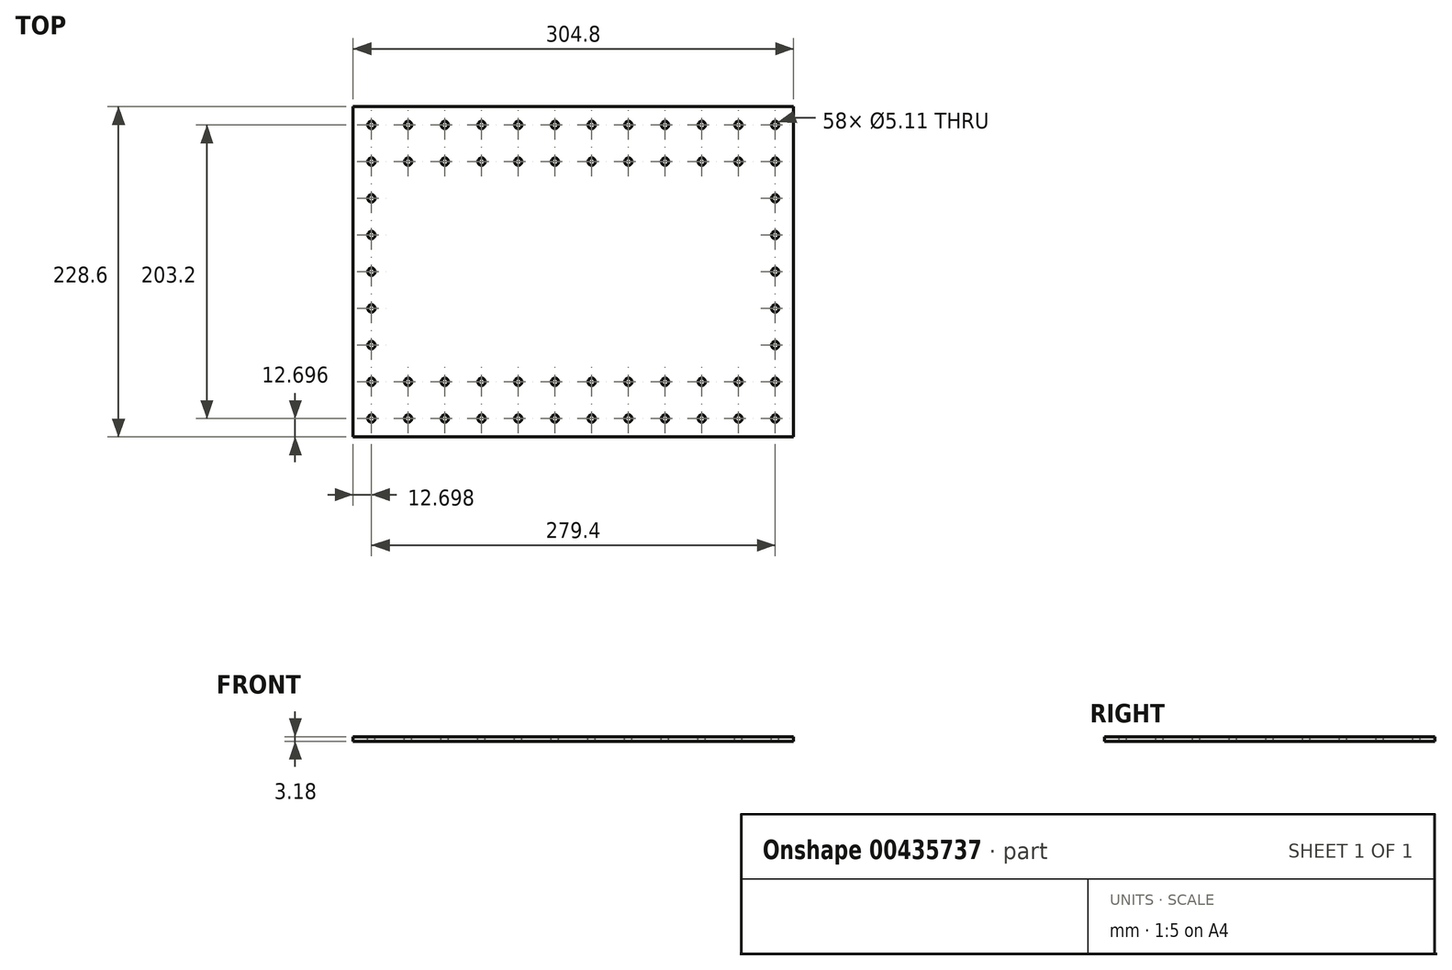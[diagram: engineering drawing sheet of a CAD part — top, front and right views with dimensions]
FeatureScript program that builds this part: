
annotation { "Feature Type Name" : "Feature", "Feature Type Description" : "" }
export const myFeature = defineFeature(function(context is Context, id is Id, definition is map)
    precondition{}
    {
        {
            var Q0;
            Q0=qCreatedBy(makeId("Top.planeOp"),FACE);
            var sketch = newSketch(context, id + "F0", { "sketchPlane" : qUnion([Q0])});
            skLineSegment(sketch, "E0.bottom", {"start": v(-91.98, 188.02) * mm, "end": v(212.82, 188.02) * mm});
            skLineSegment(sketch, "E0.top", {"start": v(-91.98, -40.58) * mm, "end": v(212.82, -40.58) * mm});
            skLineSegment(sketch, "E0.left", {"start": v(-91.98, 188.02) * mm, "end": v(-91.98, -40.58) * mm});
            skLineSegment(sketch, "E0.right", {"start": v(212.82, 188.02) * mm, "end": v(212.82, -40.58) * mm});
            skSolve(sketch);
        }
        {
            var Q0;
            Q0 = qSketchRegion(id + "F0", true);
            extrude(context, id + "F1", {"entities" : qUnion([Q0]), "depth" : 3.17 * mm});
        }
        {
            var Q0;
            Q0=makeQuery(id+"F1.opExtrude","CAP_FACE",FACE,{"disambiguationData":[OSD([sQuery(id+"F0.wireOp",EDGE,"E0.bottom"),sQuery(id+"F0.wireOp",EDGE,"E0.top"),sQuery(id+"F0.wireOp",EDGE,"E0.left"),sQuery(id+"F0.wireOp",EDGE,"E0.right")])],"isStart":false});
            var sketch = newSketch(context, id + "F2", { "sketchPlane" : qUnion([Q0])});
            skCircle(sketch, "E1", {"center": v(-79.28, 175.32) * mm, "radius": 2.55 * mm});
            skCircle(sketch, "E2.1.0.0", {"center": v(-53.88, 175.32) * mm, "radius": 2.55 * mm});
            skCircle(sketch, "E2.2.0.0", {"center": v(-28.48, 175.32) * mm, "radius": 2.55 * mm});
            skCircle(sketch, "E2.3.0.0", {"center": v(-3.08, 175.32) * mm, "radius": 2.55 * mm});
            skCircle(sketch, "E2.4.0.0", {"center": v(22.32, 175.32) * mm, "radius": 2.55 * mm});
            skCircle(sketch, "E2.5.0.0", {"center": v(47.72, 175.32) * mm, "radius": 2.55 * mm});
            skCircle(sketch, "E2.6.0.0", {"center": v(73.12, 175.32) * mm, "radius": 2.55 * mm});
            skCircle(sketch, "E2.7.0.0", {"center": v(98.52, 175.32) * mm, "radius": 2.55 * mm});
            skCircle(sketch, "E2.8.0.0", {"center": v(123.92, 175.32) * mm, "radius": 2.55 * mm});
            skCircle(sketch, "E2.9.0.0", {"center": v(149.32, 175.32) * mm, "radius": 2.55 * mm});
            skCircle(sketch, "E2.10.0.0", {"center": v(174.72, 175.32) * mm, "radius": 2.55 * mm});
            skCircle(sketch, "E2.11.0.0", {"center": v(200.12, 175.32) * mm, "radius": 2.55 * mm});
            skLineSegment(sketch, "E2.direction1", {"start": v(-79.28, 175.32) * mm, "end": v(-53.88, 175.32) * mm, "construction": true});
            skCircle(sketch, "E3.0.1.0", {"center": v(200.12, 149.92) * mm, "radius": 2.55 * mm});
            skCircle(sketch, "E3.0.2.0", {"center": v(200.12, 124.52) * mm, "radius": 2.55 * mm});
            skCircle(sketch, "E3.0.3.0", {"center": v(200.12, 99.12) * mm, "radius": 2.55 * mm});
            skCircle(sketch, "E3.0.4.0", {"center": v(200.12, 73.72) * mm, "radius": 2.55 * mm});
            skCircle(sketch, "E3.0.5.0", {"center": v(200.12, 48.32) * mm, "radius": 2.55 * mm});
            skCircle(sketch, "E3.0.6.0", {"center": v(200.12, 22.92) * mm, "radius": 2.55 * mm});
            skCircle(sketch, "E3.0.7.0", {"center": v(200.12, -2.48) * mm, "radius": 2.55 * mm});
            skCircle(sketch, "E3.0.8.0", {"center": v(200.12, -27.88) * mm, "radius": 2.55 * mm});
            skLineSegment(sketch, "E3.direction1", {"start": v(200.12, 175.32) * mm, "end": v(225.52, 175.32) * mm, "construction": true});
            skLineSegment(sketch, "E3.direction2", {"start": v(200.12, 175.32) * mm, "end": v(200.12, 149.92) * mm, "construction": true});
            skCircle(sketch, "E4.1.0.0", {"center": v(174.72, -27.88) * mm, "radius": 2.55 * mm});
            skCircle(sketch, "E4.2.0.0", {"center": v(149.32, -27.88) * mm, "radius": 2.55 * mm});
            skCircle(sketch, "E4.3.0.0", {"center": v(123.92, -27.88) * mm, "radius": 2.55 * mm});
            skCircle(sketch, "E4.4.0.0", {"center": v(98.52, -27.88) * mm, "radius": 2.55 * mm});
            skCircle(sketch, "E4.5.0.0", {"center": v(73.12, -27.88) * mm, "radius": 2.55 * mm});
            skCircle(sketch, "E4.6.0.0", {"center": v(47.72, -27.88) * mm, "radius": 2.55 * mm});
            skCircle(sketch, "E4.7.0.0", {"center": v(22.32, -27.88) * mm, "radius": 2.55 * mm});
            skCircle(sketch, "E4.8.0.0", {"center": v(-3.08, -27.88) * mm, "radius": 2.55 * mm});
            skCircle(sketch, "E4.9.0.0", {"center": v(-28.48, -27.88) * mm, "radius": 2.55 * mm});
            skCircle(sketch, "E4.10.0.0", {"center": v(-53.88, -27.88) * mm, "radius": 2.55 * mm});
            skCircle(sketch, "E4.11.0.0", {"center": v(-79.28, -27.88) * mm, "radius": 2.55 * mm});
            skLineSegment(sketch, "E4.direction1", {"start": v(200.12, -27.88) * mm, "end": v(174.72, -27.88) * mm, "construction": true});
            skCircle(sketch, "E5.0.1.0", {"center": v(-79.28, -2.48) * mm, "radius": 2.55 * mm});
            skCircle(sketch, "E5.0.2.0", {"center": v(-79.28, 22.92) * mm, "radius": 2.55 * mm});
            skCircle(sketch, "E5.0.3.0", {"center": v(-79.28, 48.32) * mm, "radius": 2.55 * mm});
            skCircle(sketch, "E5.0.4.0", {"center": v(-79.28, 73.72) * mm, "radius": 2.55 * mm});
            skCircle(sketch, "E5.0.5.0", {"center": v(-79.28, 99.12) * mm, "radius": 2.55 * mm});
            skCircle(sketch, "E5.0.6.0", {"center": v(-79.28, 124.52) * mm, "radius": 2.55 * mm});
            skCircle(sketch, "E5.0.7.0", {"center": v(-79.28, 149.92) * mm, "radius": 2.55 * mm});
            skLineSegment(sketch, "E5.direction1", {"start": v(-79.28, -27.88) * mm, "end": v(-53.88, -27.88) * mm, "construction": true});
            skLineSegment(sketch, "E5.direction2", {"start": v(-79.28, -27.88) * mm, "end": v(-79.28, -2.48) * mm, "construction": true});
            skCircle(sketch, "E6.1.0.0", {"center": v(174.72, 149.92) * mm, "radius": 2.55 * mm});
            skCircle(sketch, "E6.2.0.0", {"center": v(149.32, 149.92) * mm, "radius": 2.55 * mm});
            skCircle(sketch, "E6.3.0.0", {"center": v(123.92, 149.92) * mm, "radius": 2.55 * mm});
            skCircle(sketch, "E6.4.0.0", {"center": v(98.52, 149.92) * mm, "radius": 2.55 * mm});
            skCircle(sketch, "E6.5.0.0", {"center": v(73.12, 149.92) * mm, "radius": 2.55 * mm});
            skCircle(sketch, "E6.6.0.0", {"center": v(47.72, 149.92) * mm, "radius": 2.55 * mm});
            skCircle(sketch, "E6.7.0.0", {"center": v(22.32, 149.92) * mm, "radius": 2.55 * mm});
            skCircle(sketch, "E6.8.0.0", {"center": v(-3.08, 149.92) * mm, "radius": 2.55 * mm});
            skCircle(sketch, "E6.9.0.0", {"center": v(-28.48, 149.92) * mm, "radius": 2.55 * mm});
            skCircle(sketch, "E6.10.0.0", {"center": v(-53.88, 149.92) * mm, "radius": 2.55 * mm});
            skLineSegment(sketch, "E6.direction1", {"start": v(200.12, 149.92) * mm, "end": v(174.72, 149.92) * mm, "construction": true});
            skCircle(sketch, "E7.1.0.0", {"center": v(174.72, -2.48) * mm, "radius": 2.55 * mm});
            skCircle(sketch, "E7.2.0.0", {"center": v(149.32, -2.48) * mm, "radius": 2.55 * mm});
            skCircle(sketch, "E7.3.0.0", {"center": v(123.92, -2.48) * mm, "radius": 2.55 * mm});
            skCircle(sketch, "E7.4.0.0", {"center": v(98.52, -2.48) * mm, "radius": 2.55 * mm});
            skCircle(sketch, "E7.5.0.0", {"center": v(73.12, -2.48) * mm, "radius": 2.55 * mm});
            skCircle(sketch, "E7.6.0.0", {"center": v(47.72, -2.48) * mm, "radius": 2.55 * mm});
            skCircle(sketch, "E7.7.0.0", {"center": v(22.32, -2.48) * mm, "radius": 2.55 * mm});
            skCircle(sketch, "E7.8.0.0", {"center": v(-3.08, -2.48) * mm, "radius": 2.55 * mm});
            skCircle(sketch, "E7.9.0.0", {"center": v(-28.48, -2.48) * mm, "radius": 2.55 * mm});
            skCircle(sketch, "E7.10.0.0", {"center": v(-53.88, -2.48) * mm, "radius": 2.55 * mm});
            skLineSegment(sketch, "E7.direction1", {"start": v(200.12, -2.48) * mm, "end": v(174.72, -2.48) * mm, "construction": true});
            skSolve(sketch);
        }
        {
            var Q0;
            Q0=sQuery(id+"F2.wireOp",VERTEX,"E4.9.0.0.center");
            var Q1;
            Q1=sQuery(id+"F2.wireOp",VERTEX,"E6.4.0.0.center");
            var Q2;
            Q2=sQuery(id+"F2.wireOp",VERTEX,"E5.direction2.start");
            var Q3;
            Q3=sQuery(id+"F2.wireOp",VERTEX,"E3.0.4.0.center");
            var Q4;
            Q4=sQuery(id+"F2.wireOp",VERTEX,"E2.6.0.0.center");
            var Q5;
            Q5=sQuery(id+"F2.wireOp",VERTEX,"E2.9.0.0.center");
            var Q6;
            Q6=sQuery(id+"F2.wireOp",VERTEX,"E2.8.0.0.center");
            var Q7;
            Q7=sQuery(id+"F2.wireOp",VERTEX,"E5.direction2.end");
            var Q8;
            Q8=sQuery(id+"F2.wireOp",VERTEX,"E7.direction1.end");
            var Q9;
            Q9=sQuery(id+"F2.wireOp",VERTEX,"E3.0.7.0.center");
            var Q10;
            Q10=sQuery(id+"F2.wireOp",VERTEX,"E7.3.0.0.center");
            var Q11;
            Q11=sQuery(id+"F2.wireOp",VERTEX,"E3.0.5.0.center");
            var Q12;
            Q12=sQuery(id+"F2.wireOp",VERTEX,"E2.2.0.0.center");
            var Q13;
            Q13=sQuery(id+"F2.wireOp",VERTEX,"E7.8.0.0.center");
            var Q14;
            Q14=sQuery(id+"F2.wireOp",VERTEX,"E6.direction1.start");
            var Q15;
            Q15=sQuery(id+"F2.wireOp",VERTEX,"E4.5.0.0.center");
            var Q16;
            Q16=sQuery(id+"F2.wireOp",VERTEX,"E3.0.6.0.center");
            var Q17;
            Q17=sQuery(id+"F2.wireOp",VERTEX,"E6.7.0.0.center");
            var Q18;
            Q18=sQuery(id+"F2.wireOp",VERTEX,"E7.9.0.0.center");
            var Q19;
            Q19=sQuery(id+"F2.wireOp",VERTEX,"E4.3.0.0.center");
            var Q20;
            Q20=sQuery(id+"F2.wireOp",VERTEX,"E4.4.0.0.center");
            var Q21;
            Q21=sQuery(id+"F2.wireOp",VERTEX,"E2.7.0.0.center");
            var Q22;
            Q22=sQuery(id+"F2.wireOp",VERTEX,"E6.3.0.0.center");
            var Q23;
            Q23=sQuery(id+"F2.wireOp",VERTEX,"E1.center");
            var Q24;
            Q24=sQuery(id+"F2.wireOp",VERTEX,"E6.direction1.end");
            var Q25;
            Q25=sQuery(id+"F2.wireOp",VERTEX,"E6.10.0.0.center");
            var Q26;
            Q26=sQuery(id+"F2.wireOp",VERTEX,"E7.7.0.0.center");
            var Q27;
            Q27=sQuery(id+"F2.wireOp",VERTEX,"E5.0.4.0.center");
            var Q28;
            Q28=sQuery(id+"F2.wireOp",VERTEX,"E6.2.0.0.center");
            var Q29;
            Q29=sQuery(id+"F2.wireOp",VERTEX,"E5.0.2.0.center");
            var Q30;
            Q30=sQuery(id+"F2.wireOp",VERTEX,"E4.6.0.0.center");
            var Q31;
            Q31=sQuery(id+"F2.wireOp",VERTEX,"E3.0.2.0.center");
            var Q32;
            Q32=sQuery(id+"F2.wireOp",VERTEX,"E5.0.5.0.center");
            var Q33;
            Q33=sQuery(id+"F2.wireOp",VERTEX,"E4.1.0.0.center");
            var Q34;
            Q34=sQuery(id+"F2.wireOp",VERTEX,"E2.4.0.0.center");
            var Q35;
            Q35=sQuery(id+"F2.wireOp",VERTEX,"E6.6.0.0.center");
            var Q36;
            Q36=sQuery(id+"F2.wireOp",VERTEX,"E3.direction2.start");
            var Q37;
            Q37=sQuery(id+"F2.wireOp",VERTEX,"E6.8.0.0.center");
            var Q38;
            Q38=sQuery(id+"F2.wireOp",VERTEX,"E7.6.0.0.center");
            var Q39;
            Q39=sQuery(id+"F2.wireOp",VERTEX,"E4.10.0.0.center");
            var Q40;
            Q40=sQuery(id+"F2.wireOp",VERTEX,"E7.2.0.0.center");
            var Q41;
            Q41=sQuery(id+"F2.wireOp",VERTEX,"E7.5.0.0.center");
            var Q42;
            Q42=sQuery(id+"F2.wireOp",VERTEX,"E4.7.0.0.center");
            var Q43;
            Q43=sQuery(id+"F2.wireOp",VERTEX,"E5.0.6.0.center");
            var Q44;
            Q44=sQuery(id+"F2.wireOp",VERTEX,"E3.0.3.0.center");
            var Q45;
            Q45=sQuery(id+"F2.wireOp",VERTEX,"E2.10.0.0.center");
            var Q46;
            Q46=sQuery(id+"F2.wireOp",VERTEX,"E7.10.0.0.center");
            var Q47;
            Q47=sQuery(id+"F2.wireOp",VERTEX,"E2.direction1.end");
            var Q48;
            Q48=sQuery(id+"F2.wireOp",VERTEX,"E5.0.3.0.center");
            var Q49;
            Q49=sQuery(id+"F2.wireOp",VERTEX,"E3.0.8.0.center");
            var Q50;
            Q50=sQuery(id+"F2.wireOp",VERTEX,"E7.4.0.0.center");
            var Q51;
            Q51=sQuery(id+"F2.wireOp",VERTEX,"E4.8.0.0.center");
            var Q52;
            Q52=sQuery(id+"F2.wireOp",VERTEX,"E6.9.0.0.center");
            var Q53;
            Q53=sQuery(id+"F2.wireOp",VERTEX,"E2.5.0.0.center");
            var Q54;
            Q54=sQuery(id+"F2.wireOp",VERTEX,"E4.2.0.0.center");
            var Q55;
            Q55=sQuery(id+"F2.wireOp",VERTEX,"E2.3.0.0.center");
            var Q56;
            Q56=sQuery(id+"F2.wireOp",VERTEX,"E5.0.7.0.center");
            var Q57;
            Q57=sQuery(id+"F2.wireOp",VERTEX,"E6.5.0.0.center");
            var Q58;
            Q58=makeQuery(id+"F1.opExtrude","SWEPT_BODY",BODY,{"disambiguationData":[OSD([sQuery(id+"F0.wireOp",EDGE,"E0.bottom"),sQuery(id+"F0.wireOp",EDGE,"E0.top"),sQuery(id+"F0.wireOp",EDGE,"E0.left"),sQuery(id+"F0.wireOp",EDGE,"E0.right")])]});
            hole(context, id + "F3", {"style" : HoleStyle.SIMPLE, "endStyle" : HoleEndStyle.THROUGH, "holeDiameter" : 5.1 * mm, "isTappedThrough" : true, "tappedDepth" : 12.7 * mm, "tapClearance" : 3, "locations" : qUnion([Q0, Q1, Q2, Q3, Q4, Q5, Q6, Q7, Q8, Q9, Q10, Q11, Q12, Q13, Q14, Q15, Q16, Q17, Q18, Q19, Q20, Q21, Q22, Q23, Q24, Q25, Q26, Q27, Q28, Q29, Q30, Q31, Q32, Q33, Q34, Q35, Q36, Q37, Q38, Q39, Q40, Q41, Q42, Q43, Q44, Q45, Q46, Q47, Q48, Q49, Q50, Q51, Q52, Q53, Q54, Q55, Q56, Q57]), "scope" : qUnion([Q58])});
        }
    });
